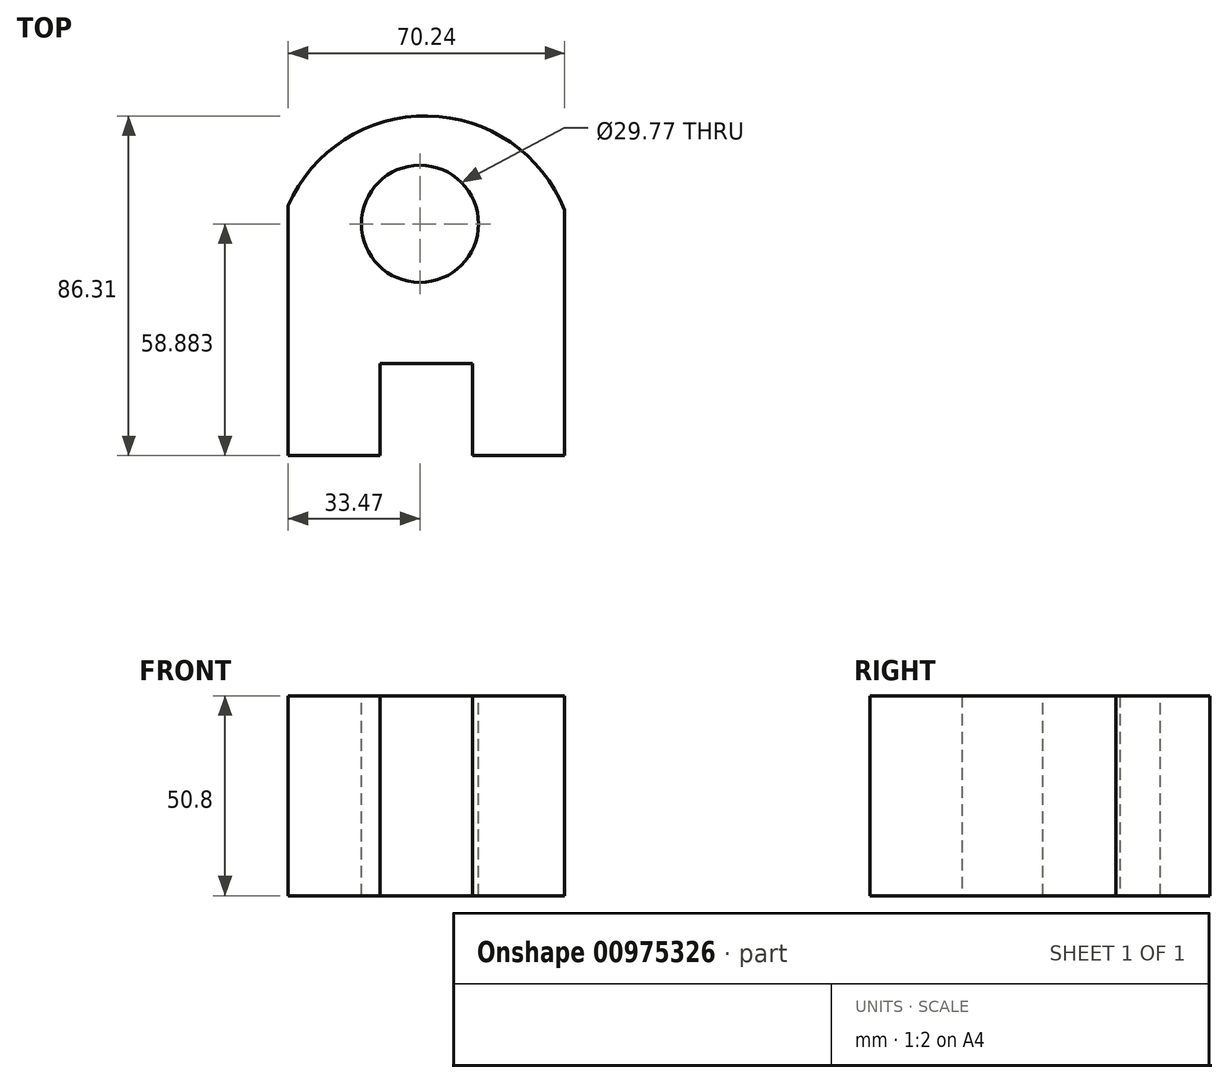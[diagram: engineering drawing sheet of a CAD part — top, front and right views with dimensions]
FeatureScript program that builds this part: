
annotation { "Feature Type Name" : "Feature", "Feature Type Description" : "" }
export const myFeature = defineFeature(function(context is Context, id is Id, definition is map)
    precondition{}
    {
        {
            var Q0;
            Q0=qCreatedBy(makeId("Top.planeOp"),FACE);
            var sketch = newSketch(context, id + "F0", { "sketchPlane" : qUnion([Q0])});
            skArc(sketch, "E0", {"start": v(36.77, 27.47) * mm, "mid": v(2, 51.34) * mm, "end": v(-33.47, 28.54) * mm});
            skLineSegment(sketch, "E1", {"start": v(-33.47, 28.54) * mm, "end": v(-33.47, -34.97) * mm});
            skLineSegment(sketch, "E2", {"start": v(-33.47, -34.97) * mm, "end": v(-10.06, -34.97) * mm});
            skLineSegment(sketch, "E3", {"start": v(-10.06, -34.97) * mm, "end": v(-10.06, -11.55) * mm});
            skLineSegment(sketch, "E4", {"start": v(-10.06, -11.55) * mm, "end": v(13.36, -11.55) * mm});
            skLineSegment(sketch, "E5", {"start": v(13.36, -11.55) * mm, "end": v(13.36, -34.97) * mm});
            skLineSegment(sketch, "E6", {"start": v(13.36, -34.97) * mm, "end": v(36.77, -34.97) * mm});
            skLineSegment(sketch, "E7", {"start": v(36.77, -34.97) * mm, "end": v(36.77, 27.47) * mm});
            skSolve(sketch);
        }
        {
            var Q0;
            Q0=makeQuery(id+"F0.imprint","IMPRINT",FACE,{"disambiguationData":[TD([[makeQuery(id+"F0.imprint","IMPRINT",EDGE,{"derivedFrom":sQuery(id+"F0.wireOp",EDGE,"E0")}),1.0]])]});
            extrude(context, id + "F1", {"entities" : qUnion([Q0]), "depth" : 25.4 * mm, "offsetDistance" : 25.4 * mm});
        }
        {
            var Q0;
            Q0=makeQuery(id+"F1.opExtrude","CAP_FACE",FACE,{"disambiguationData":[OSD([sQuery(id+"F0.wireOp",EDGE,"E0"),sQuery(id+"F0.wireOp",EDGE,"E1"),sQuery(id+"F0.wireOp",EDGE,"E2"),sQuery(id+"F0.wireOp",EDGE,"E3"),sQuery(id+"F0.wireOp",EDGE,"E4"),sQuery(id+"F0.wireOp",EDGE,"E5"),sQuery(id+"F0.wireOp",EDGE,"E6"),sQuery(id+"F0.wireOp",EDGE,"E7")])],"isStart":false});
            extrude(context, id + "F2", {"entities" : qUnion([Q0]), "operationType" : NewBodyOperationType.ADD, "depth" : 25.4 * mm, "offsetDistance" : 25.4 * mm});
        }
        {
            var Q0;
            Q0=makeQuery(id+"F2.opExtrude","CAP_FACE",FACE,{"disambiguationData":[OSD([sQuery(id+"F0.wireOp",EDGE,"E0"),sQuery(id+"F0.wireOp",EDGE,"E1"),sQuery(id+"F0.wireOp",EDGE,"E2"),sQuery(id+"F0.wireOp",EDGE,"E3"),sQuery(id+"F0.wireOp",EDGE,"E4"),sQuery(id+"F0.wireOp",EDGE,"E5"),sQuery(id+"F0.wireOp",EDGE,"E6"),sQuery(id+"F0.wireOp",EDGE,"E7")])],"isStart":false});
            var sketch = newSketch(context, id + "F3", { "sketchPlane" : qUnion([Q0])});
            skCircle(sketch, "E8", {"center": v(0, 23.91) * mm, "radius": 14.88 * mm});
            skSolve(sketch);
        }
        {
            var Q0;
            Q0=makeQuery(id+"F3.imprint","IMPRINT",FACE,{"disambiguationData":[TD([[makeQuery(id+"F3.imprint","IMPRINT",EDGE,{"derivedFrom":sQuery(id+"F3.wireOp",EDGE,"E8")}),1.0]])]});
            extrude(context, id + "F4", {"entities" : qUnion([Q0]), "operationType" : NewBodyOperationType.REMOVE, "endBound" : BoundingType.THROUGH_ALL, "oppositeDirection" : true, "depth" : 25.4 * mm, "offsetDistance" : 25.4 * mm});
        }
    });
